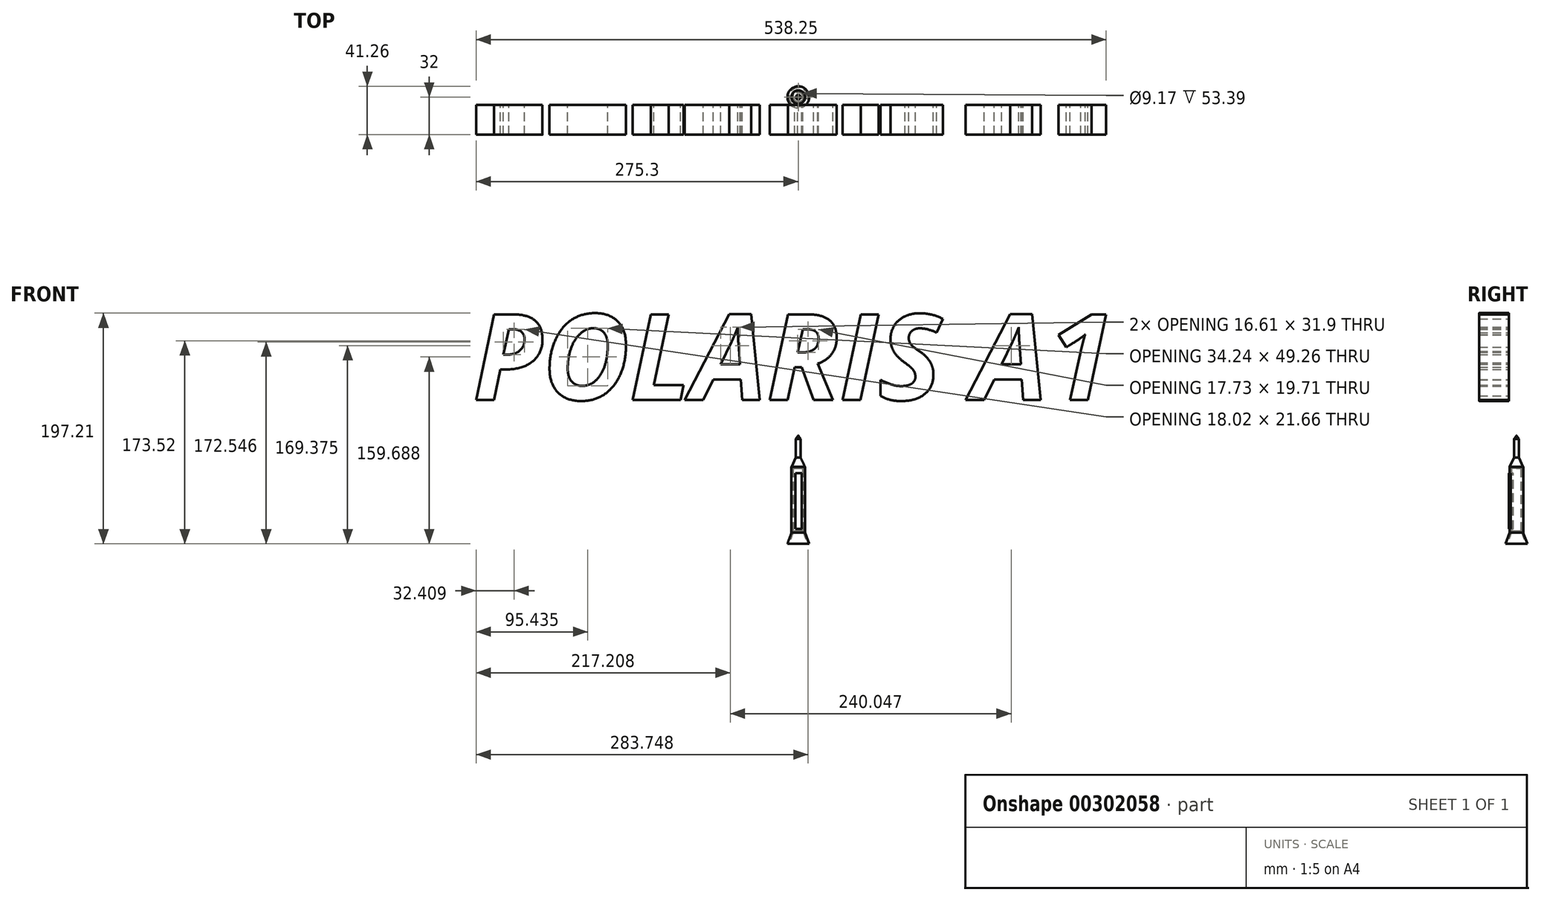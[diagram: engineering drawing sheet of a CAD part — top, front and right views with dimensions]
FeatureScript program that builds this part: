
annotation { "Feature Type Name" : "Feature", "Feature Type Description" : "" }
export const myFeature = defineFeature(function(context is Context, id is Id, definition is map)
    precondition{}
    {
        {
            var Q0;
            Q0=qCreatedBy(makeId("Front.planeOp"),FACE);
            var sketch = newSketch(context, id + "F0", { "sketchPlane" : qUnion([Q0])});
            skLineSegment(sketch, "E0", {"start": v(0, 0) * mm, "end": v(-5.85, 0) * mm});
            skLineSegment(sketch, "E1", {"start": v(-5.85, 0) * mm, "end": v(-5.85, 55.93) * mm});
            skLineSegment(sketch, "E2", {"start": v(-5.85, 55.93) * mm, "end": v(0, 55.93) * mm});
            skLineSegment(sketch, "E3", {"start": v(0, 55.93) * mm, "end": v(0, 0) * mm});
            skSolve(sketch);
        }
        {
            var Q0;
            Q0 = qSketchRegion(id + "F0", true);
            var Q1;
            Q1=sQuery(id+"F0.wireOp",EDGE,"E3");
            revolve(context, id + "F1", {"entities" : qUnion([Q0]), "axis" : qUnion([Q1]), "revolveType" : RevolveType.FULL});
        }
        {
            var Q0;
            Q0=qCreatedBy(makeId("Front.planeOp"),FACE);
            var sketch = newSketch(context, id + "F2", { "sketchPlane" : qUnion([Q0])});
            skLineSegment(sketch, "E4", {"start": v(-5.71, 55.98) * mm, "end": v(-1.97, 64.03) * mm});
            skLineSegment(sketch, "E5", {"start": v(-1.97, 64.03) * mm, "end": v(0, 64.03) * mm});
            skLineSegment(sketch, "E6", {"start": v(0, 64.03) * mm, "end": v(0, 55.98) * mm});
            skLineSegment(sketch, "E7", {"start": v(0, 55.98) * mm, "end": v(-5.71, 55.98) * mm});
            skSolve(sketch);
        }
        {
            var Q0;
            Q0 = qSketchRegion(id + "F2", true);
            var Q1;
            Q1=sQuery(id+"F2.wireOp",EDGE,"E6");
            revolve(context, id + "F3", {"entities" : qUnion([Q0]), "axis" : qUnion([Q1]), "revolveType" : RevolveType.FULL});
        }
        {
            var Q0;
            Q0=qCreatedBy(makeId("Front.planeOp"),FACE);
            var sketch = newSketch(context, id + "F4", { "sketchPlane" : qUnion([Q0])});
            skLineSegment(sketch, "E8", {"start": v(0, 64.03) * mm, "end": v(-1.96, 64.03) * mm});
            skLineSegment(sketch, "E9", {"start": v(-1.96, 64.03) * mm, "end": v(-1.96, 79.96) * mm});
            skLineSegment(sketch, "E10", {"start": v(-1.96, 79.96) * mm, "end": v(0, 79.96) * mm});
            skLineSegment(sketch, "E11", {"start": v(0, 79.96) * mm, "end": v(0, 64.03) * mm});
            skSolve(sketch);
        }
        {
            var Q0;
            Q0 = qSketchRegion(id + "F4", true);
            var Q1;
            Q1=sQuery(id+"F4.wireOp",EDGE,"E11");
            revolve(context, id + "F5", {"operationType" : NewBodyOperationType.ADD, "entities" : qUnion([Q0]), "axis" : qUnion([Q1]), "revolveType" : RevolveType.FULL});
        }
        {
            var Q0;
            Q0=qCreatedBy(makeId("Front.planeOp"),FACE);
            var sketch = newSketch(context, id + "F6", { "sketchPlane" : qUnion([Q0])});
            skLineSegment(sketch, "E12", {"start": v(-1.96, 79.96) * mm, "end": v(-0.54, 82.06) * mm});
            skLineSegment(sketch, "E13", {"start": v(-0.54, 82.06) * mm, "end": v(0, 82.06) * mm});
            skLineSegment(sketch, "E14", {"start": v(0, 82.06) * mm, "end": v(0, 79.96) * mm});
            skLineSegment(sketch, "E15", {"start": v(0, 79.96) * mm, "end": v(-1.96, 79.96) * mm});
            skSolve(sketch);
        }
        {
            var Q0;
            Q0 = qSketchRegion(id + "F6", true);
            var Q1;
            Q1=sQuery(id+"F6.wireOp",EDGE,"E14");
            revolve(context, id + "F7", {"operationType" : NewBodyOperationType.ADD, "entities" : qUnion([Q0]), "axis" : qUnion([Q1]), "revolveType" : RevolveType.FULL});
        }
        {
            var Q0;
            Q0=makeQuery(id+"F7.opRevolve","SWEPT_FACE",FACE,{"disambiguationData":[OSD([sQuery(id+"F6.wireOp",EDGE,"E13")])]});
            var sketch = newSketch(context, id + "F8", { "sketchPlane" : qUnion([Q0])});
            skArc(sketch, "E16", {"start": v(0, 0.54) * mm, "mid": v(-0.54, 0) * mm, "end": v(0, -0.54) * mm});
            skLineSegment(sketch, "E17", {"start": v(0, 0.54) * mm, "end": v(0, -0.54) * mm});
            skSolve(sketch);
        }
        {
            var Q0;
            Q0 = qSketchRegion(id + "F8", true);
            var Q1;
            Q1=sQuery(id+"F8.wireOp",EDGE,"E17");
            revolve(context, id + "F9", {"operationType" : NewBodyOperationType.ADD, "entities" : qUnion([Q0]), "axis" : qUnion([Q1]), "revolveType" : RevolveType.FULL});
        }
        {
            var Q0;
            Q0=qCreatedBy(makeId("Front.planeOp"),FACE);
            var sketch = newSketch(context, id + "F10", { "sketchPlane" : qUnion([Q0])});
            skLineSegment(sketch, "E18", {"start": v(0, 0) * mm, "end": v(-5.7, 0) * mm});
            skLineSegment(sketch, "E19", {"start": v(-5.7, 0) * mm, "end": v(-9.26, -9.82) * mm});
            skLineSegment(sketch, "E20", {"start": v(-9.26, -9.82) * mm, "end": v(0, -9.82) * mm});
            skLineSegment(sketch, "E21", {"start": v(0, -9.82) * mm, "end": v(0, 0) * mm});
            skSolve(sketch);
        }
        {
            var Q0;
            Q0 = qSketchRegion(id + "F10", true);
            var Q1;
            Q1=sQuery(id+"F10.wireOp",EDGE,"E21");
            revolve(context, id + "F11", {"operationType" : NewBodyOperationType.ADD, "entities" : qUnion([Q0]), "axis" : qUnion([Q1]), "revolveType" : RevolveType.FULL});
        }
        {
            var Q0;
            Q0=makeQuery(id+"F11.opRevolve","SWEPT_FACE",FACE,{"disambiguationData":[OSD([sQuery(id+"F10.wireOp",EDGE,"E20")])]});
            shell(context, id + "F12", {"entities" : qUnion([Q0]), "thickness" : 1.27 * mm});
        }
        {
            var Q0;
            Q0=makeQuery(id+"F12.opShell","OFFSET_FACE",FACE,{"disambiguationData":[OSD([sQuery(id+"F0.wireOp",EDGE,"E2")])]});
            var sketch = newSketch(context, id + "F13", { "sketchPlane" : qUnion([Q0])});
            skCircle(sketch, "E22", {"center": v(0, 0) * mm, "radius": 3.9 * mm});
            skSolve(sketch);
        }
        {
            var Q0;
            Q0 = qSketchRegion(id + "F13", true);
            extrude(context, id + "F14", {"entities" : qUnion([Q0]), "operationType" : NewBodyOperationType.ADD, "depth" : 53.85 * mm});
        }
        {
            var Q0;
            Q0=qCreatedBy(makeId("Front.planeOp"),FACE);
            var sketch = newSketch(context, id + "F15", { "sketchPlane" : qUnion([Q0])});
            skLineSegment(sketch, "E23.bottom", {"start": v(-2.44, 50.52) * mm, "end": v(2.97, 50.52) * mm});
            skLineSegment(sketch, "E23.top", {"start": v(-2.44, 2.88) * mm, "end": v(2.97, 2.88) * mm});
            skLineSegment(sketch, "E23.left", {"start": v(-2.44, 50.52) * mm, "end": v(-2.44, 2.88) * mm});
            skLineSegment(sketch, "E23.right", {"start": v(2.97, 50.52) * mm, "end": v(2.97, 2.88) * mm});
            skSolve(sketch);
        }
        {
            var Q0;
            Q0 = qSketchRegion(id + "F15", true);
            extrude(context, id + "F16", {"entities" : qUnion([Q0]), "operationType" : NewBodyOperationType.ADD, "depth" : 6.6 * mm});
        }
        {
            var Q0;
            Q0=makeQuery(id+"F16.opExtrude","CAP_FACE",FACE,{"disambiguationData":[OSD([sQuery(id+"F15.wireOp",EDGE,"E23.bottom"),sQuery(id+"F15.wireOp",EDGE,"E23.top"),sQuery(id+"F15.wireOp",EDGE,"E23.left"),sQuery(id+"F15.wireOp",EDGE,"E23.right")])],"isStart":false});
            var sketch = newSketch(context, id + "F17", { "sketchPlane" : qUnion([Q0])});
            skText(sketch, "E24", { "text": "POLARIS A1", "fontName": "OpenSans-BoldItalic.ttf"});
            const initialGuessF17  = {"E24": [-0.27795, 0.11326, 1, 0, 0.0736]};
            skSetInitialGuess(sketch, initialGuessF17);
            skSolve(sketch);
        }
        {
            var Q0;
            Q0 = qSketchRegion(id + "F17", true);
            extrude(context, id + "F18", {"entities" : qUnion([Q0]), "depth" : 25.4 * mm});
        }
    });
